# Revit family: GNW_A3-AW-11-Timber-Architrave-(NZ)
name_source: partatom
category: Windows
revit_build: Autodesk Revit 2016 (Build: 20150220_1215(x64)
units: mm (PartAtom-declared; Revit-internal decimal feet)

## family parameters
Always vertical = Yes
Cut with Voids When Loaded = No
Host = Wall
Room Calculation Point = No
Shared = No

## types (5) — shared parameters
Construction Type = Timber
CoverBd_Offset = 5 mm  [stored 0.0164042 ft]
CoverBd_Width = 45 mm  [stored 0.147638 ft]
JambRebate = 20 mm  [stored 0.0656168 ft]
Operation = DoublePanelVertical
Packer = 25 mm  [stored 0.082021 ft]
Structural Tolerance = 5 mm  [stored 0.0164042 ft]
Wall Closure = By host

## per-type parameters (varying)
| type | Keynote | Rough Width | Width |
| 1400 x 1200 Timber | 45-13-005 | 1210 mm  [stored 3.96982 ft] | 1200 mm |
| 1200 x 1000 Timber | 45-13-003 | 1010 mm | 1000 mm  [stored 3.28084 ft] |
| 1400 x 1600 Timber | 45-13-006 | 1610 mm  [stored 5.28215 ft] | 1600 mm  [stored 5.24934 ft] |
| 1200 x 1800 Timber | 45-13-004 | 1810 mm  [stored 5.93832 ft] | 1800 mm  [stored 5.90551 ft] |
| 1000 x 1200 Timber | 45-13-002 | 1210 mm  [stored 3.96982 ft] | 1200 mm |

note: [stored X ft] marks values corroborated as IEEE doubles in the binary element streams (Revit-internal decimal feet)

## geometry (parser evidence)
native form markers: Sweep x1
no freeform markers — native parametric forms only
